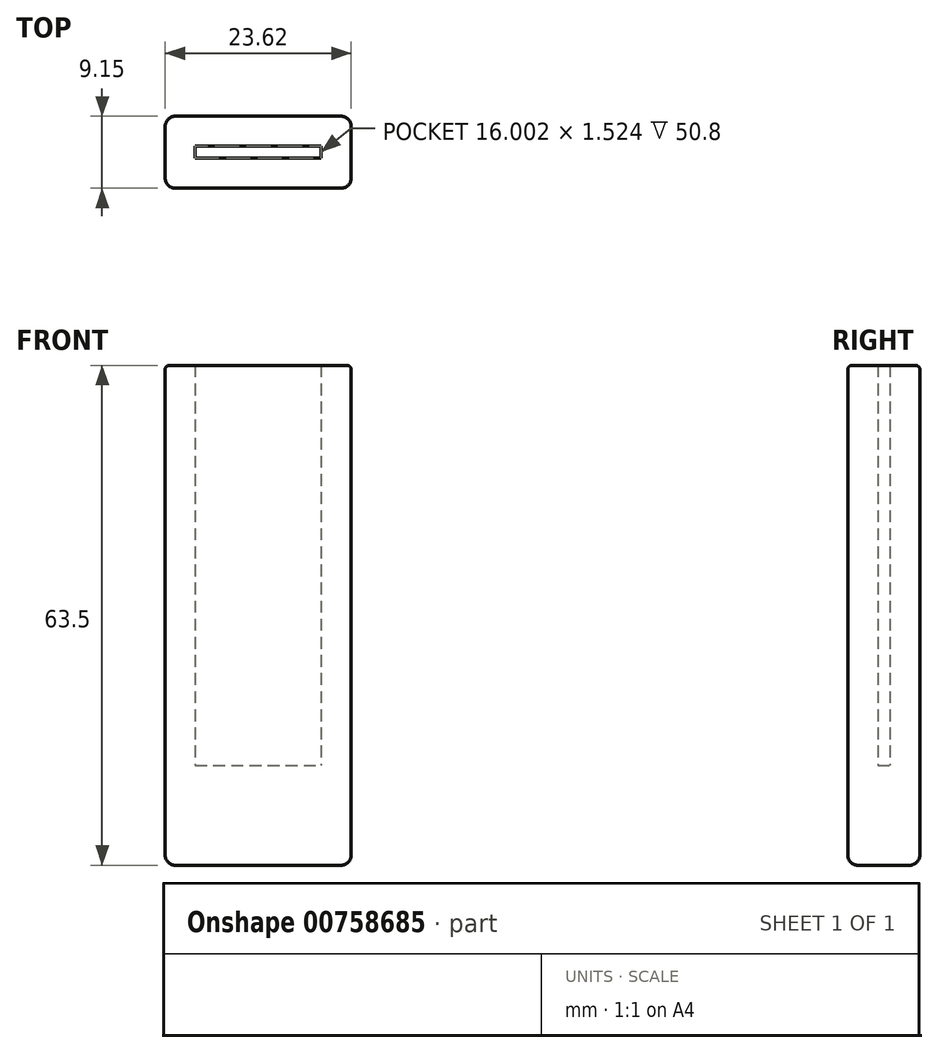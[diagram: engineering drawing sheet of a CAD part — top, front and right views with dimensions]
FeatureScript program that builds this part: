
annotation { "Feature Type Name" : "Feature", "Feature Type Description" : "" }
export const myFeature = defineFeature(function(context is Context, id is Id, definition is map)
    precondition{}
    {
        {
            var Q0;
            Q0=qCreatedBy(makeId("Top.planeOp"),FACE);
            var sketch = newSketch(context, id + "F0", { "sketchPlane" : qUnion([Q0])});
            skLineSegment(sketch, "E0.bottom", {"start": v(3.25, -26.69) * mm, "end": v(-20.37, -26.69) * mm});
            skLineSegment(sketch, "E0.top", {"start": v(3.25, -17.54) * mm, "end": v(-20.37, -17.54) * mm});
            skLineSegment(sketch, "E0.left", {"start": v(3.25, -26.69) * mm, "end": v(3.25, -17.54) * mm});
            skLineSegment(sketch, "E0.right", {"start": v(-20.37, -26.69) * mm, "end": v(-20.37, -17.54) * mm});
            skSolve(sketch);
        }
        {
            var Q0;
            Q0=makeQuery(id+"F0.imprint","IMPRINT",FACE,{"disambiguationData":[TD([[makeQuery(id+"F0.imprint","IMPRINT",EDGE,{"derivedFrom":sQuery(id+"F0.wireOp",EDGE,"E0.bottom")}),-1.0]])]});
            extrude(context, id + "F1", {"entities" : qUnion([Q0]), "depth" : 12.7 * mm, "offsetDistance" : 25.4 * mm});
        }
        {
            var Q0;
            Q0=makeQuery(id+"FoRw4XYYdB1lv1c_2.boolean.opBoolean","MERGE",EDGE,{"derivedFrom":[makeQuery(id+"F1.opExtrude","SWEPT_EDGE",EDGE,{"disambiguationData":[OSD([sQuery(id+"F0.wireOp",EDGE,"E0.top"),sQuery(id+"F0.wireOp",EDGE,"E0.right")])]}),makeQuery(id+"FoRw4XYYdB1lv1c_2.opExtrude","SWEPT_EDGE",EDGE,{"disambiguationData":[OSD([sQuery(id+"Fr3hN15bfvRdWDK_2.wireOp",EDGE,"CZNW2gms-Sh0r-61UB-tCEm-EGkg1MaxKw1d.bottom"),sQuery(id+"Fr3hN15bfvRdWDK_2.wireOp",EDGE,"CZNW2gms-Sh0r-61UB-tCEm-EGkg1MaxKw1d.left")])]})]});
            var Q1;
            Q1=makeQuery(id+"FoRw4XYYdB1lv1c_2.boolean.opBoolean","MERGE",EDGE,{"derivedFrom":[makeQuery(id+"F1.opExtrude","SWEPT_EDGE",EDGE,{"disambiguationData":[OSD([sQuery(id+"F0.wireOp",EDGE,"E0.top"),sQuery(id+"F0.wireOp",EDGE,"E0.left")])]}),makeQuery(id+"FoRw4XYYdB1lv1c_2.opExtrude","SWEPT_EDGE",EDGE,{"disambiguationData":[OSD([sQuery(id+"Fr3hN15bfvRdWDK_2.wireOp",EDGE,"CZNW2gms-Sh0r-61UB-tCEm-EGkg1MaxKw1d.bottom"),sQuery(id+"Fr3hN15bfvRdWDK_2.wireOp",EDGE,"CZNW2gms-Sh0r-61UB-tCEm-EGkg1MaxKw1d.right")])]})]});
            var Q2;
            Q2=makeQuery(id+"FoRw4XYYdB1lv1c_2.boolean.opBoolean","MERGE",EDGE,{"derivedFrom":[makeQuery(id+"F1.opExtrude","SWEPT_EDGE",EDGE,{"disambiguationData":[OSD([sQuery(id+"F0.wireOp",EDGE,"E0.bottom"),sQuery(id+"F0.wireOp",EDGE,"E0.left")])]}),makeQuery(id+"FoRw4XYYdB1lv1c_2.opExtrude","SWEPT_EDGE",EDGE,{"disambiguationData":[OSD([sQuery(id+"Fr3hN15bfvRdWDK_2.wireOp",EDGE,"CZNW2gms-Sh0r-61UB-tCEm-EGkg1MaxKw1d.top"),sQuery(id+"Fr3hN15bfvRdWDK_2.wireOp",EDGE,"CZNW2gms-Sh0r-61UB-tCEm-EGkg1MaxKw1d.right")])]})]});
            var Q3;
            Q3=makeQuery(id+"FoRw4XYYdB1lv1c_2.boolean.opBoolean","MERGE",EDGE,{"derivedFrom":[makeQuery(id+"F1.opExtrude","SWEPT_EDGE",EDGE,{"disambiguationData":[OSD([sQuery(id+"F0.wireOp",EDGE,"E0.bottom"),sQuery(id+"F0.wireOp",EDGE,"E0.right")])]}),makeQuery(id+"FoRw4XYYdB1lv1c_2.opExtrude","SWEPT_EDGE",EDGE,{"disambiguationData":[OSD([sQuery(id+"Fr3hN15bfvRdWDK_2.wireOp",EDGE,"CZNW2gms-Sh0r-61UB-tCEm-EGkg1MaxKw1d.top"),sQuery(id+"Fr3hN15bfvRdWDK_2.wireOp",EDGE,"CZNW2gms-Sh0r-61UB-tCEm-EGkg1MaxKw1d.left")])]})]});
            var Q4;
            Q4=makeQuery(id+"F1.opExtrude","CAP_EDGE",EDGE,{"disambiguationData":[OSD([sQuery(id+"F0.wireOp",EDGE,"E0.bottom")])],"isStart":true});
            var Q5;
            Q5=makeQuery(id+"F1.opExtrude","CAP_EDGE",EDGE,{"disambiguationData":[OSD([sQuery(id+"F0.wireOp",EDGE,"E0.right")])],"isStart":true});
            var Q6;
            Q6=makeQuery(id+"F1.opExtrude","CAP_EDGE",EDGE,{"disambiguationData":[OSD([sQuery(id+"F0.wireOp",EDGE,"E0.top")])],"isStart":true});
            var Q7;
            Q7=makeQuery(id+"F1.opExtrude","CAP_EDGE",EDGE,{"disambiguationData":[OSD([sQuery(id+"F0.wireOp",EDGE,"E0.left")])],"isStart":true});
            var Q8;
            Q8=makeQuery(id+"FoRw4XYYdB1lv1c_2.opExtrude","CAP_EDGE",EDGE,{"disambiguationData":[OSD([sQuery(id+"Fr3hN15bfvRdWDK_2.wireOp",EDGE,"CZNW2gms-Sh0r-61UB-tCEm-EGkg1MaxKw1d.bottom")])],"isStart":false});
            var Q9;
            Q9=makeQuery(id+"FoRw4XYYdB1lv1c_2.opExtrude","CAP_EDGE",EDGE,{"disambiguationData":[OSD([sQuery(id+"Fr3hN15bfvRdWDK_2.wireOp",EDGE,"CZNW2gms-Sh0r-61UB-tCEm-EGkg1MaxKw1d.top")])],"isStart":false});
            var Q10;
            Q10=makeQuery(id+"FoRw4XYYdB1lv1c_2.opExtrude","CAP_EDGE",EDGE,{"disambiguationData":[OSD([sQuery(id+"Fr3hN15bfvRdWDK_2.wireOp",EDGE,"CZNW2gms-Sh0r-61UB-tCEm-EGkg1MaxKw1d.left")])],"isStart":false});
            var Q11;
            Q11=makeQuery(id+"FoRw4XYYdB1lv1c_2.opExtrude","CAP_EDGE",EDGE,{"disambiguationData":[OSD([sQuery(id+"Fr3hN15bfvRdWDK_2.wireOp",EDGE,"CZNW2gms-Sh0r-61UB-tCEm-EGkg1MaxKw1d.right")])],"isStart":false});
            fillet(context, id + "F2", {"entities" : qUnion([Q0, Q1, Q2, Q3, Q4, Q5, Q6, Q7, Q8, Q9, Q10, Q11]), "radius" : 1.27 * mm, "tangentPropagation" : true, "allowEdgeOverflow" : false});
        }
        {
            var Q0;
            Q0=makeQuery(id+"F1.opExtrude","CAP_FACE",FACE,{"disambiguationData":[OSD([sQuery(id+"F0.wireOp",EDGE,"E0.bottom"),sQuery(id+"F0.wireOp",EDGE,"E0.top"),sQuery(id+"F0.wireOp",EDGE,"E0.left"),sQuery(id+"F0.wireOp",EDGE,"E0.right")])],"isStart":false});
            var sketch = newSketch(context, id + "F3", { "sketchPlane" : qUnion([Q0])});
            skLineSegment(sketch, "E1.bottom", {"start": v(-16.56, -22.88) * mm, "end": v(-0.56, -22.88) * mm});
            skLineSegment(sketch, "E1.top", {"start": v(-16.56, -21.35) * mm, "end": v(-0.56, -21.35) * mm});
            skLineSegment(sketch, "E1.left", {"start": v(-16.56, -22.88) * mm, "end": v(-16.56, -21.35) * mm});
            skLineSegment(sketch, "E1.right", {"start": v(-0.56, -22.88) * mm, "end": v(-0.56, -21.35) * mm});
            skPoint(sketch, "E1.middle", {"position": v(-8.56, -22.11) * mm});
            skPoint(sketch, "E1.middle.positionSnap0", {"position": v(-20.37, -22.11) * mm});
            skPoint(sketch, "E1.middle.positionSnap1", {"position": v(-8.56, -17.54) * mm});
            skPoint(sketch, "E1.centerSnap0", {"position": v(-20.37, -22.11) * mm});
            skPoint(sketch, "E1.centerSnap1", {"position": v(-8.56, -17.54) * mm});
            skSolve(sketch);
        }
        {
            var Q0;
            Q0=makeQuery(id+"F3.imprint","IMPRINT",FACE,{"disambiguationData":[TD([[makeQuery(id+"F3.imprint","IMPRINT",EDGE,{"derivedFrom":sQuery(id+"F3.wireOp",EDGE,"E1.bottom")}),-1.0]])]});
            extrude(context, id + "F4", {"entities" : qUnion([Q0]), "operationType" : NewBodyOperationType.ADD, "depth" : 50.8 * mm, "offsetDistance" : 25.4 * mm});
        }
        {
            var Q0;
            Q0=makeQuery(id+"F4.opExtrude","CAP_EDGE",EDGE,{"disambiguationData":[OSD([sQuery(id+"F0.wireOp",EDGE,"E0.top")])],"isStart":false});
            var Q1;
            Q1=makeQuery(id+"F4.opExtrude","CAP_EDGE",EDGE,{"disambiguationData":[OSD([sQuery(id+"F0.wireOp",EDGE,"E0.left")])],"isStart":false});
            var Q2;
            {var subQ0=sQuery(id+"F0.wireOp",EDGE,"E0.right");var subQ1=sQuery(id+"F0.wireOp",EDGE,"E0.left");var subQ2=sQuery(id+"F0.wireOp",EDGE,"E0.top");var subQ3=sQuery(id+"F0.wireOp",EDGE,"E0.bottom");Q2=makeQuery(id+"F4.opExtrude","CAP_EDGE",EDGE,{"disambiguationData":[OSD([subQ3,subQ2,subQ1,subQ0]),TDD([makeQuery(id+"F3.imprint","IMPRINT",EDGE,{"derivedFrom":makeQuery(id+"F2.opFillet","BLEND_EDGE",EDGE,{"blendedFrom":[makeQuery(id+"F1.opExtrude","SWEPT_EDGE",EDGE,{"disambiguationData":[OSD([subQ2,subQ1])]}),makeQuery(id+"F1.opExtrude","CAP_FACE",FACE,{"disambiguationData":[OSD([subQ3,subQ2,subQ1,subQ0])],"isStart":false})],"blendedInto":[makeQuery(id+"F1.opExtrude","CAP_FACE",FACE,{"disambiguationData":[OSD([subQ3,subQ2,subQ1,subQ0])],"isStart":false})]})})])],"isStart":false});}
            var Q3;
            {var subQ0=sQuery(id+"F0.wireOp",EDGE,"E0.right");var subQ1=sQuery(id+"F0.wireOp",EDGE,"E0.left");var subQ2=sQuery(id+"F0.wireOp",EDGE,"E0.top");var subQ3=sQuery(id+"F0.wireOp",EDGE,"E0.bottom");Q3=makeQuery(id+"F4.opExtrude","CAP_EDGE",EDGE,{"disambiguationData":[OSD([subQ3,subQ2,subQ1,subQ0]),TDD([makeQuery(id+"F3.imprint","IMPRINT",EDGE,{"derivedFrom":makeQuery(id+"F2.opFillet","BLEND_EDGE",EDGE,{"blendedFrom":[makeQuery(id+"F1.opExtrude","SWEPT_EDGE",EDGE,{"disambiguationData":[OSD([subQ3,subQ1])]}),makeQuery(id+"F1.opExtrude","CAP_FACE",FACE,{"disambiguationData":[OSD([subQ3,subQ2,subQ1,subQ0])],"isStart":false})],"blendedInto":[makeQuery(id+"F1.opExtrude","CAP_FACE",FACE,{"disambiguationData":[OSD([subQ3,subQ2,subQ1,subQ0])],"isStart":false})]})})])],"isStart":false});}
            var Q4;
            Q4=makeQuery(id+"F4.opExtrude","CAP_EDGE",EDGE,{"disambiguationData":[OSD([sQuery(id+"F0.wireOp",EDGE,"E0.bottom")])],"isStart":false});
            var Q5;
            {var subQ0=sQuery(id+"F0.wireOp",EDGE,"E0.right");var subQ1=sQuery(id+"F0.wireOp",EDGE,"E0.left");var subQ2=sQuery(id+"F0.wireOp",EDGE,"E0.top");var subQ3=sQuery(id+"F0.wireOp",EDGE,"E0.bottom");Q5=makeQuery(id+"F4.opExtrude","CAP_EDGE",EDGE,{"disambiguationData":[OSD([subQ3,subQ2,subQ1,subQ0]),TDD([makeQuery(id+"F3.imprint","IMPRINT",EDGE,{"derivedFrom":makeQuery(id+"F2.opFillet","BLEND_EDGE",EDGE,{"blendedFrom":[makeQuery(id+"F1.opExtrude","SWEPT_EDGE",EDGE,{"disambiguationData":[OSD([subQ3,subQ0])]}),makeQuery(id+"F1.opExtrude","CAP_FACE",FACE,{"disambiguationData":[OSD([subQ3,subQ2,subQ1,subQ0])],"isStart":false})],"blendedInto":[makeQuery(id+"F1.opExtrude","CAP_FACE",FACE,{"disambiguationData":[OSD([subQ3,subQ2,subQ1,subQ0])],"isStart":false})]})})])],"isStart":false});}
            var Q6;
            Q6=makeQuery(id+"F4.opExtrude","CAP_EDGE",EDGE,{"disambiguationData":[OSD([sQuery(id+"F0.wireOp",EDGE,"E0.right")])],"isStart":false});
            var Q7;
            {var subQ0=sQuery(id+"F0.wireOp",EDGE,"E0.right");var subQ1=sQuery(id+"F0.wireOp",EDGE,"E0.left");var subQ2=sQuery(id+"F0.wireOp",EDGE,"E0.top");var subQ3=sQuery(id+"F0.wireOp",EDGE,"E0.bottom");Q7=makeQuery(id+"F4.opExtrude","CAP_EDGE",EDGE,{"disambiguationData":[OSD([subQ3,subQ2,subQ1,subQ0]),TDD([makeQuery(id+"F3.imprint","IMPRINT",EDGE,{"derivedFrom":makeQuery(id+"F2.opFillet","BLEND_EDGE",EDGE,{"blendedFrom":[makeQuery(id+"F1.opExtrude","SWEPT_EDGE",EDGE,{"disambiguationData":[OSD([subQ2,subQ0])]}),makeQuery(id+"F1.opExtrude","CAP_FACE",FACE,{"disambiguationData":[OSD([subQ3,subQ2,subQ1,subQ0])],"isStart":false})],"blendedInto":[makeQuery(id+"F1.opExtrude","CAP_FACE",FACE,{"disambiguationData":[OSD([subQ3,subQ2,subQ1,subQ0])],"isStart":false})]})})])],"isStart":false});}
            fillet(context, id + "F5", {"entities" : qUnion([Q0, Q1, Q2, Q3, Q4, Q5, Q6, Q7]), "radius" : 0.5 * mm, "tangentPropagation" : true, "allowEdgeOverflow" : false});
        }
    });
